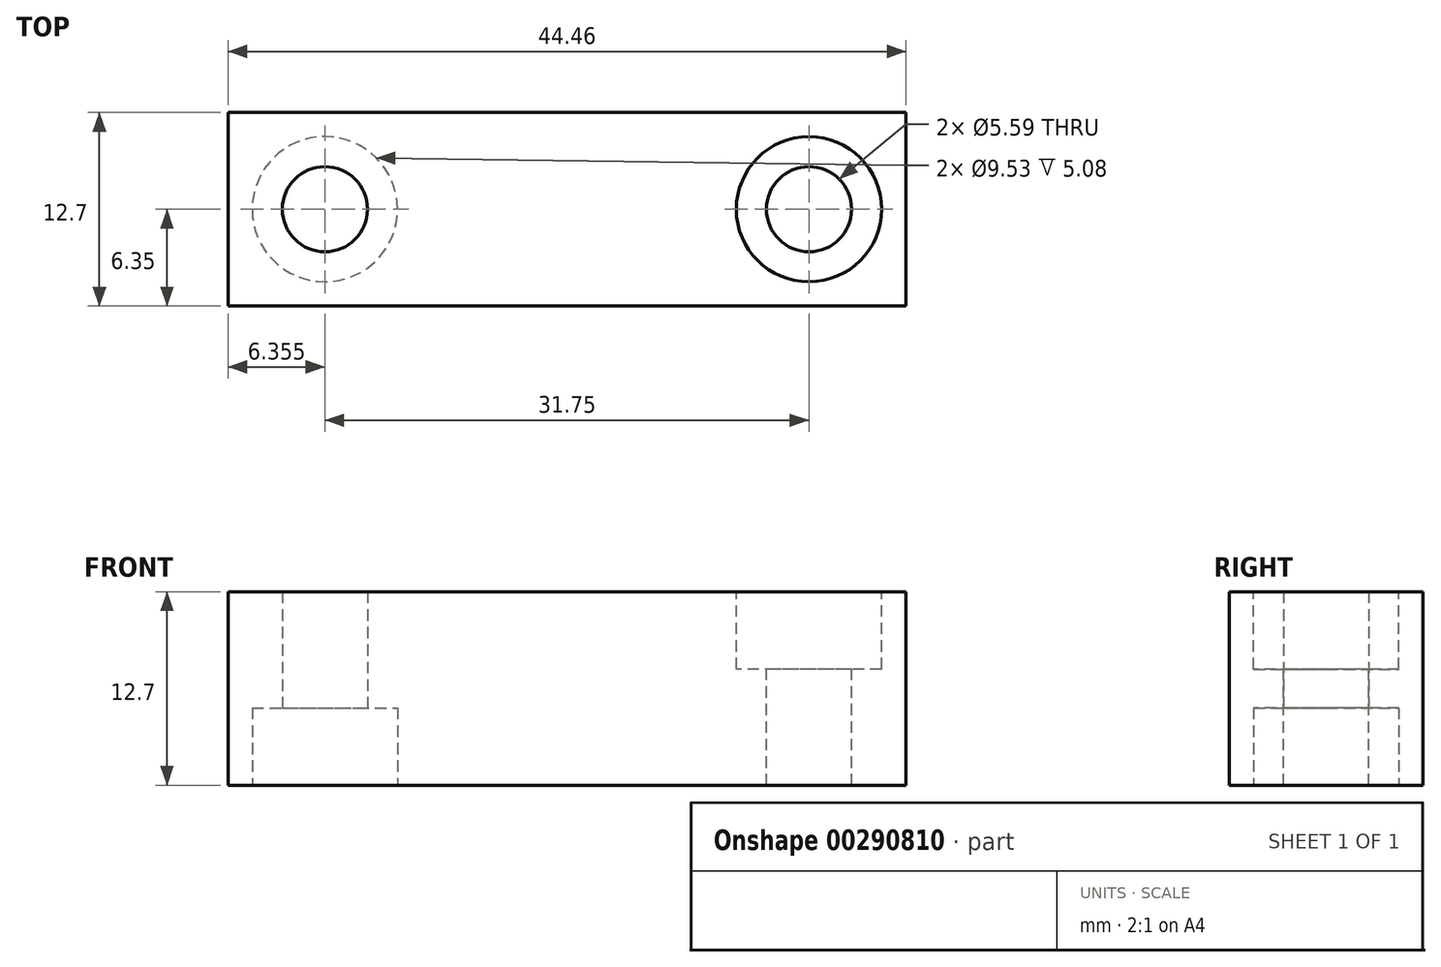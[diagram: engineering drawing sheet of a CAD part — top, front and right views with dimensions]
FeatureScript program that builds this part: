
annotation { "Feature Type Name" : "Feature", "Feature Type Description" : "" }
export const myFeature = defineFeature(function(context is Context, id is Id, definition is map)
    precondition{}
    {
        {
            var Q0;
            Q0=qCreatedBy(makeId("Top.planeOp"),FACE);
            var sketch = newSketch(context, id + "F0", { "sketchPlane" : qUnion([Q0])});
            skLineSegment(sketch, "E0.bottom", {"start": v(-22.22, 0) * mm, "end": v(22.22, 0) * mm});
            skLineSegment(sketch, "E0.top", {"start": v(-22.22, -12.7) * mm, "end": v(22.23, -12.7) * mm});
            skLineSegment(sketch, "E0.left", {"start": v(-22.22, 0) * mm, "end": v(-22.22, -12.7) * mm});
            skLineSegment(sketch, "E0.right", {"start": v(22.22, 0) * mm, "end": v(22.22, -12.7) * mm});
            skSolve(sketch);
        }
        {
            var Q0;
            Q0 = qSketchRegion(id + "F0", true);
            extrude(context, id + "F1", {"entities" : qUnion([Q0]), "depth" : 12.7 * mm});
        }
        {
            var Q0;
            Q0=makeQuery(id+"F1.opExtrude","CAP_FACE",FACE,{"disambiguationData":[OSD([sQuery(id+"F0.wireOp",EDGE,"E0.bottom"),sQuery(id+"F0.wireOp",EDGE,"E0.top"),sQuery(id+"F0.wireOp",EDGE,"E0.left"),sQuery(id+"F0.wireOp",EDGE,"E0.right")])],"isStart":false});
            var sketch = newSketch(context, id + "F2", { "sketchPlane" : qUnion([Q0])});
            skCircle(sketch, "E1", {"center": v(15.87, -6.35) * mm, "radius": 2.8 * mm});
            skSolve(sketch);
        }
        {
            var Q0;
            Q0 = qSketchRegion(id + "F2", true);
            extrude(context, id + "F3", {"entities" : qUnion([Q0]), "operationType" : NewBodyOperationType.REMOVE, "endBound" : BoundingType.THROUGH_ALL, "oppositeDirection" : true, "depth" : 6.35 * mm});
        }
        {
            var Q0;
            Q0=makeQuery(id+"F1.opExtrude","CAP_FACE",FACE,{"disambiguationData":[OSD([sQuery(id+"F0.wireOp",EDGE,"E0.bottom"),sQuery(id+"F0.wireOp",EDGE,"E0.top"),sQuery(id+"F0.wireOp",EDGE,"E0.left"),sQuery(id+"F0.wireOp",EDGE,"E0.right")])],"isStart":true});
            var sketch = newSketch(context, id + "F4", { "sketchPlane" : qUnion([Q0])});
            skCircle(sketch, "E2", {"center": v(-15.87, 6.35) * mm, "radius": 2.8 * mm});
            skSolve(sketch);
        }
        {
            var Q0;
            Q0 = qSketchRegion(id + "F4", true);
            extrude(context, id + "F5", {"entities" : qUnion([Q0]), "operationType" : NewBodyOperationType.REMOVE, "endBound" : BoundingType.THROUGH_ALL, "oppositeDirection" : true, "depth" : 6.35 * mm});
        }
        {
            var Q0;
            Q0=makeQuery(id+"F2.imprint","IMPRINT",FACE,{"disambiguationData":[TD([[makeQuery(id+"F2.imprint","IMPRINT",EDGE,{"derivedFrom":sQuery(id+"F2.wireOp",EDGE,"E1")}),-1.0]])]});
            var sketch = newSketch(context, id + "F6", { "sketchPlane" : qUnion([Q0])});
            skCircle(sketch, "E3", {"center": v(15.87, -6.35) * mm, "radius": 4.76 * mm});
            skSolve(sketch);
        }
        {
            var Q0;
            Q0 = qSketchRegion(id + "F6", true);
            extrude(context, id + "F7", {"entities" : qUnion([Q0]), "operationType" : NewBodyOperationType.REMOVE, "oppositeDirection" : true, "depth" : 5.08 * mm});
        }
        {
            var Q0;
            Q0=makeQuery(id+"F4.imprint","IMPRINT",FACE,{"disambiguationData":[TD([[makeQuery(id+"F4.imprint","IMPRINT",EDGE,{"derivedFrom":sQuery(id+"F4.wireOp",EDGE,"E2")}),-1.0]])]});
            var sketch = newSketch(context, id + "F8", { "sketchPlane" : qUnion([Q0])});
            skCircle(sketch, "E4", {"center": v(-15.87, 6.35) * mm, "radius": 4.76 * mm});
            skSolve(sketch);
        }
        {
            var Q0;
            Q0 = qSketchRegion(id + "F8", true);
            extrude(context, id + "F9", {"entities" : qUnion([Q0]), "operationType" : NewBodyOperationType.REMOVE, "oppositeDirection" : true, "depth" : 5.08 * mm});
        }
    });
